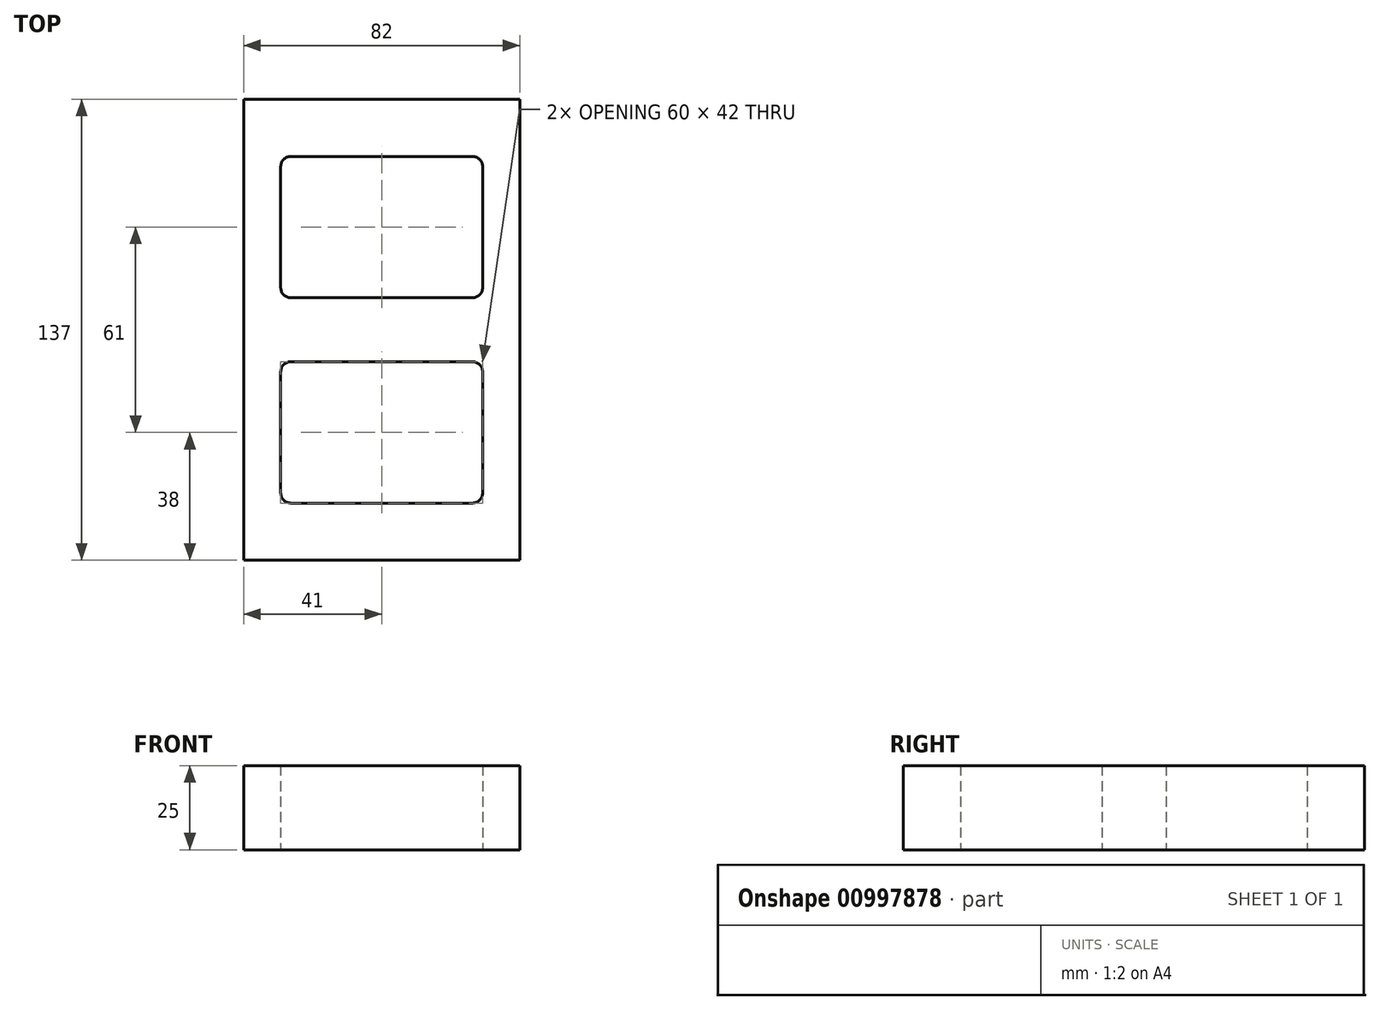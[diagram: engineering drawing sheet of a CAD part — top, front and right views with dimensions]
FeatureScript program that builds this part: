
annotation { "Feature Type Name" : "Feature", "Feature Type Description" : "" }
export const myFeature = defineFeature(function(context is Context, id is Id, definition is map)
    precondition{}
    {
        {
            var Q0;
            Q0=qCreatedBy(makeId("Top.planeOp"),FACE);
            var sketch = newSketch(context, id + "F0", { "sketchPlane" : qUnion([Q0])});
            skLineSegment(sketch, "E0.bottom", {"start": v(0, 0) * mm, "end": v(82, 0) * mm});
            skLineSegment(sketch, "E0.top", {"start": v(0, 137) * mm, "end": v(82, 137) * mm});
            skLineSegment(sketch, "E0.left", {"start": v(0, 0) * mm, "end": v(0, 137) * mm});
            skLineSegment(sketch, "E0.right", {"start": v(82, 0) * mm, "end": v(82, 137) * mm});
            skLineSegment(sketch, "E1.bottom", {"start": v(14, 17) * mm, "end": v(68, 17) * mm});
            skLineSegment(sketch, "E1.top", {"start": v(14, 59) * mm, "end": v(68, 59) * mm});
            skLineSegment(sketch, "E1.left", {"start": v(11, 20) * mm, "end": v(11, 56) * mm});
            skLineSegment(sketch, "E1.right", {"start": v(71, 20) * mm, "end": v(71, 56) * mm});
            skPoint(sketch, "E2.visualSharp", {"position": v(11, 59) * mm});
            skArc(sketch, "E2.filletArc", {"start": v(14, 59) * mm, "mid": v(11.88, 58.12) * mm, "end": v(11, 56) * mm});
            skPoint(sketch, "E3.visualSharp", {"position": v(71, 59) * mm});
            skArc(sketch, "E3.filletArc", {"start": v(71, 56) * mm, "mid": v(70.12, 58.12) * mm, "end": v(68, 59) * mm});
            skPoint(sketch, "E4.visualSharp", {"position": v(71, 17) * mm});
            skArc(sketch, "E4.filletArc", {"start": v(68, 17) * mm, "mid": v(70.12, 17.88) * mm, "end": v(71, 20) * mm});
            skPoint(sketch, "E5.visualSharp", {"position": v(11, 17) * mm});
            skArc(sketch, "E5.filletArc", {"start": v(11, 20) * mm, "mid": v(11.88, 17.88) * mm, "end": v(14, 17) * mm});
            skLineSegment(sketch, "E6.bottom", {"start": v(14, 120) * mm, "end": v(68, 120) * mm});
            skLineSegment(sketch, "E6.top", {"start": v(14, 78) * mm, "end": v(68, 78) * mm});
            skLineSegment(sketch, "E6.left", {"start": v(11, 117) * mm, "end": v(11, 81) * mm});
            skLineSegment(sketch, "E6.right", {"start": v(71, 117) * mm, "end": v(71, 81) * mm});
            skPoint(sketch, "E7.visualSharp", {"position": v(71, 120) * mm});
            skArc(sketch, "E7.filletArc", {"start": v(71, 117) * mm, "mid": v(70.12, 119.12) * mm, "end": v(68, 120) * mm});
            skPoint(sketch, "E8.visualSharp", {"position": v(71, 78) * mm});
            skArc(sketch, "E8.filletArc", {"start": v(68, 78) * mm, "mid": v(70.12, 78.88) * mm, "end": v(71, 81) * mm});
            skPoint(sketch, "E9.visualSharp", {"position": v(11, 78) * mm});
            skArc(sketch, "E9.filletArc", {"start": v(11, 81) * mm, "mid": v(11.88, 78.88) * mm, "end": v(14, 78) * mm});
            skPoint(sketch, "E10.visualSharp", {"position": v(11, 120) * mm});
            skArc(sketch, "E10.filletArc", {"start": v(14, 120) * mm, "mid": v(11.88, 119.12) * mm, "end": v(11, 117) * mm});
            skSolve(sketch);
        }
        {
            var Q0;
            Q0=makeQuery(id+"F0.imprint","IMPRINT",FACE,{"disambiguationData":[TD([[makeQuery(id+"F0.imprint","IMPRINT",EDGE,{"derivedFrom":sQuery(id+"F0.wireOp",EDGE,"E0.bottom")}),1.0]])]});
            extrude(context, id + "F1", {"entities" : qUnion([Q0]), "depth" : 25 * mm, "offsetDistance" : 25 * mm});
        }
    });
